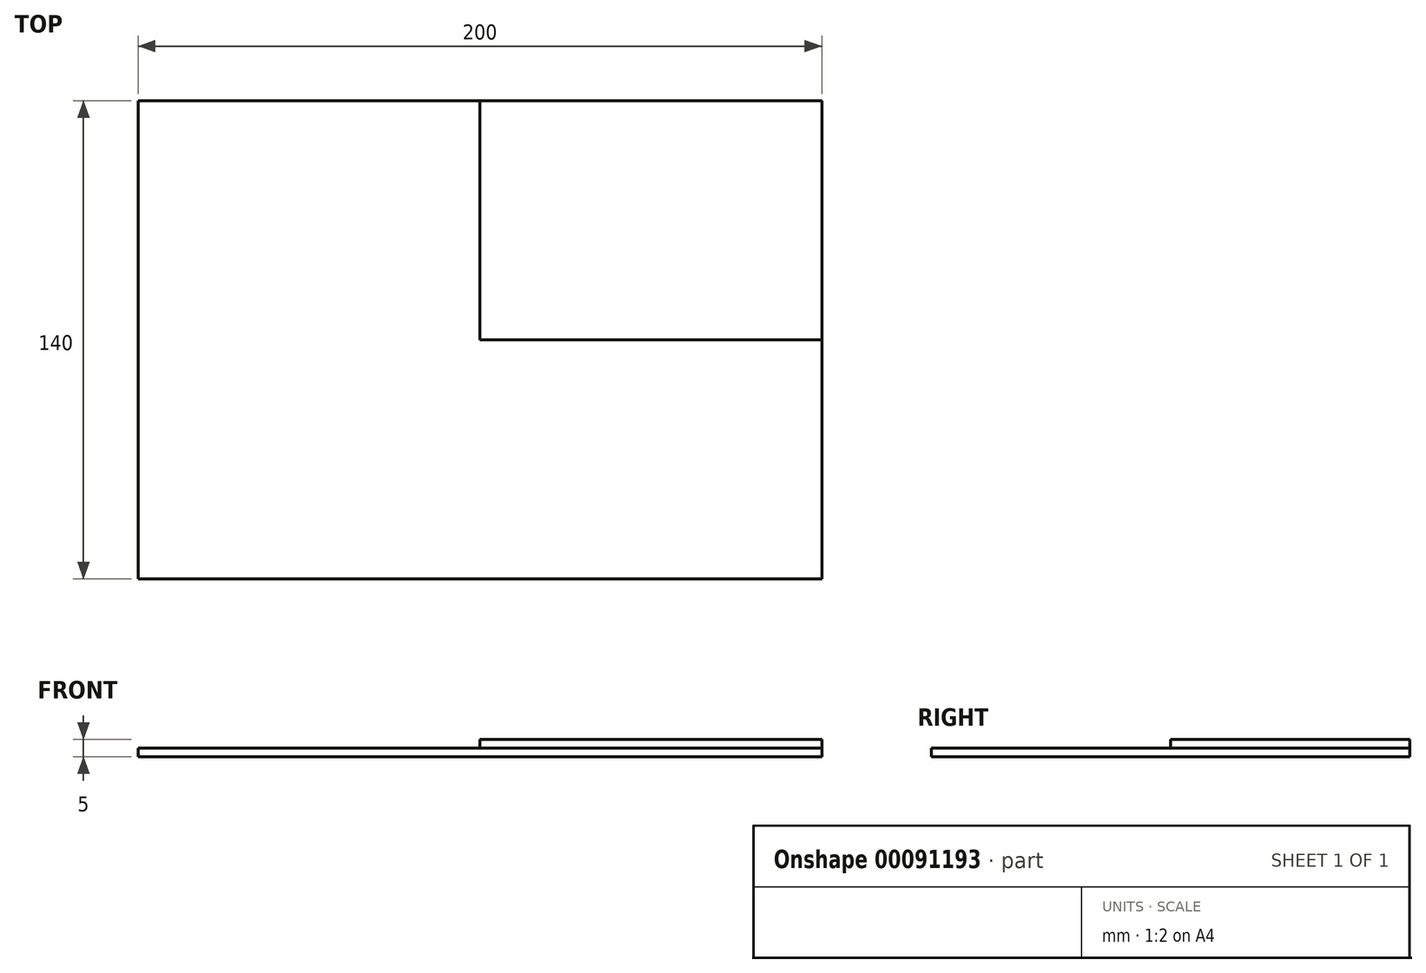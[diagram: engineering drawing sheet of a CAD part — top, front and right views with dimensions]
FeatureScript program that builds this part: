
annotation { "Feature Type Name" : "Feature", "Feature Type Description" : "" }
export const myFeature = defineFeature(function(context is Context, id is Id, definition is map)
    precondition{}
    {
        {
            var Q0;
            Q0=qCreatedBy(makeId("Top.planeOp"),FACE);
            var sketch = newSketch(context, id + "F0", { "sketchPlane" : qUnion([Q0])});
            skLineSegment(sketch, "E0.left", {"start": v(-40.6, -15.45) * mm, "end": v(-40.6, -18.65) * mm});
            skLineSegment(sketch, "E0.right", {"start": v(-34.2, -15.45) * mm, "end": v(-34.2, -18.65) * mm});
            skLineSegment(sketch, "E1.left", {"start": v(-21.4, -15.45) * mm, "end": v(-21.4, -18.65) * mm});
            skLineSegment(sketch, "E1.right", {"start": v(-15, -15.45) * mm, "end": v(-15, -18.65) * mm});
            skLineSegment(sketch, "E2.bottom", {"start": v(100, -70) * mm, "end": v(-100, -70) * mm});
            skLineSegment(sketch, "E2.top", {"start": v(100, 70) * mm, "end": v(-100, 70) * mm});
            skLineSegment(sketch, "E2.left", {"start": v(100, -70) * mm, "end": v(100, 70) * mm});
            skLineSegment(sketch, "E2.right", {"start": v(-100, -70) * mm, "end": v(-100, 70) * mm});
            skPoint(sketch, "E2.middle", {"position": v(0, 0) * mm});
            skSolve(sketch);
        }
        {
            var Q0;
            Q0=qSketchRegion(id+"F0",true);
            extrude(context, id + "F1", {"entities" : qUnion([Q0]), "depth" : 2.5 * mm});
        }
        {
            var Q0;
            Q0=makeQuery(id+"F1.opExtrude","CAP_FACE",FACE,{"disambiguationData":[OSD([sQuery(id+"F0.wireOp",EDGE,"g2GRYD4u-kQ1t-d2H4-DUDK-qeszsydTZ718.bottom"),sQuery(id+"F0.wireOp",EDGE,"g2GRYD4u-kQ1t-d2H4-DUDK-qeszsydTZ718.top"),sQuery(id+"F0.wireOp",EDGE,"g2GRYD4u-kQ1t-d2H4-DUDK-qeszsydTZ718.left"),sQuery(id+"F0.wireOp",EDGE,"g2GRYD4u-kQ1t-d2H4-DUDK-qeszsydTZ718.right"),sQuery(id+"F0.wireOp",EDGE,"F9jM45aM-hXXd-Ke85-cE65-kxFD46mlW0e7.bottom"),sQuery(id+"F0.wireOp",EDGE,"F9jM45aM-hXXd-Ke85-cE65-kxFD46mlW0e7.top"),sQuery(id+"F0.wireOp",EDGE,"F9jM45aM-hXXd-Ke85-cE65-kxFD46mlW0e7.left"),sQuery(id+"F0.wireOp",EDGE,"F9jM45aM-hXXd-Ke85-cE65-kxFD46mlW0e7.right"),sQuery(id+"F0.wireOp",EDGE,"E0.bottom"),sQuery(id+"F0.wireOp",EDGE,"E0.top"),sQuery(id+"F0.wireOp",EDGE,"E0.left"),sQuery(id+"F0.wireOp",EDGE,"E0.right"),sQuery(id+"F0.wireOp",EDGE,"E1.bottom"),sQuery(id+"F0.wireOp",EDGE,"E1.top"),sQuery(id+"F0.wireOp",EDGE,"E1.left"),sQuery(id+"F0.wireOp",EDGE,"E1.right"),sQuery(id+"F0.wireOp",EDGE,"gYRwMo5l-9Btb-rEzc-mIL0-1baufJ4tWouF.bottom"),sQuery(id+"F0.wireOp",EDGE,"gYRwMo5l-9Btb-rEzc-mIL0-1baufJ4tWouF.top"),sQuery(id+"F0.wireOp",EDGE,"gYRwMo5l-9Btb-rEzc-mIL0-1baufJ4tWouF.left"),sQuery(id+"F0.wireOp",EDGE,"gYRwMo5l-9Btb-rEzc-mIL0-1baufJ4tWouF.right"),sQuery(id+"F0.wireOp",EDGE,"E2.bottom"),sQuery(id+"F0.wireOp",EDGE,"E2.top"),sQuery(id+"F0.wireOp",EDGE,"E2.left"),sQuery(id+"F0.wireOp",EDGE,"E2.right")])],"isStart":false});
            var sketch = newSketch(context, id + "F2", { "sketchPlane" : qUnion([Q0])});
            skLineSegment(sketch, "E3.bottom", {"start": v(0, 0) * mm, "end": v(200, 0) * mm});
            skLineSegment(sketch, "E3.top", {"start": v(0, 140) * mm, "end": v(200, 140) * mm});
            skLineSegment(sketch, "E3.left", {"start": v(0, 0) * mm, "end": v(0, 140) * mm});
            skLineSegment(sketch, "E3.right", {"start": v(200, 0) * mm, "end": v(200, 140) * mm});
            skSolve(sketch);
        }
        {
            var Q0;
            {var subQ0=sQuery(id+"F2.wireOp",EDGE,"E3.left");var subQ1=sQuery(id+"F2.wireOp",EDGE,"E3.bottom");var subQ2=makeQuery(id+"F2.imprint","INTERSECT",VERTEX,{"derivedFrom":[subQ1,subQ0]});Q0=makeQuery(id+"F2.imprint","IMPRINT",FACE,{"disambiguationData":[TD([[makeQuery(id+"F2.imprint","IMPRINT",EDGE,{"disambiguationData":[TD([[subQ2,-1.0]])],"derivedFrom":subQ1}),1.0]])]});}
            var Q1;
            {var subQ5=makeQuery(id+"F1.opExtrude","CAP_EDGE",EDGE,{"disambiguationData":[OSD([sQuery(id+"F0.wireOp",EDGE,"gYRwMo5l-9Btb-rEzc-mIL0-1baufJ4tWouF.bottom")])],"isStart":false});Q1=makeQuery(id+"F2.imprint","IMPRINT",FACE,{"disambiguationData":[TD([[makeQuery(id+"F2.imprint","IMPRINT",EDGE,{"derivedFrom":subQ5}),-1.0]])]});}
            var Q2;
            {var subQ7=makeQuery(id+"F1.opExtrude","CAP_EDGE",EDGE,{"disambiguationData":[OSD([sQuery(id+"F0.wireOp",EDGE,"gYRwMo5l-9Btb-rEzc-mIL0-1baufJ4tWouF.bottom")])],"isStart":false});Q2=makeQuery(id+"F2.imprint","IMPRINT",FACE,{"disambiguationData":[TD([[makeQuery(id+"F2.imprint","IMPRINT",EDGE,{"derivedFrom":subQ7}),1.0]])]});}
            extrude(context, id + "F3", {"entities" : qUnion([Q0, Q1, Q2]), "depth" : 2.5 * mm});
        }
    });
